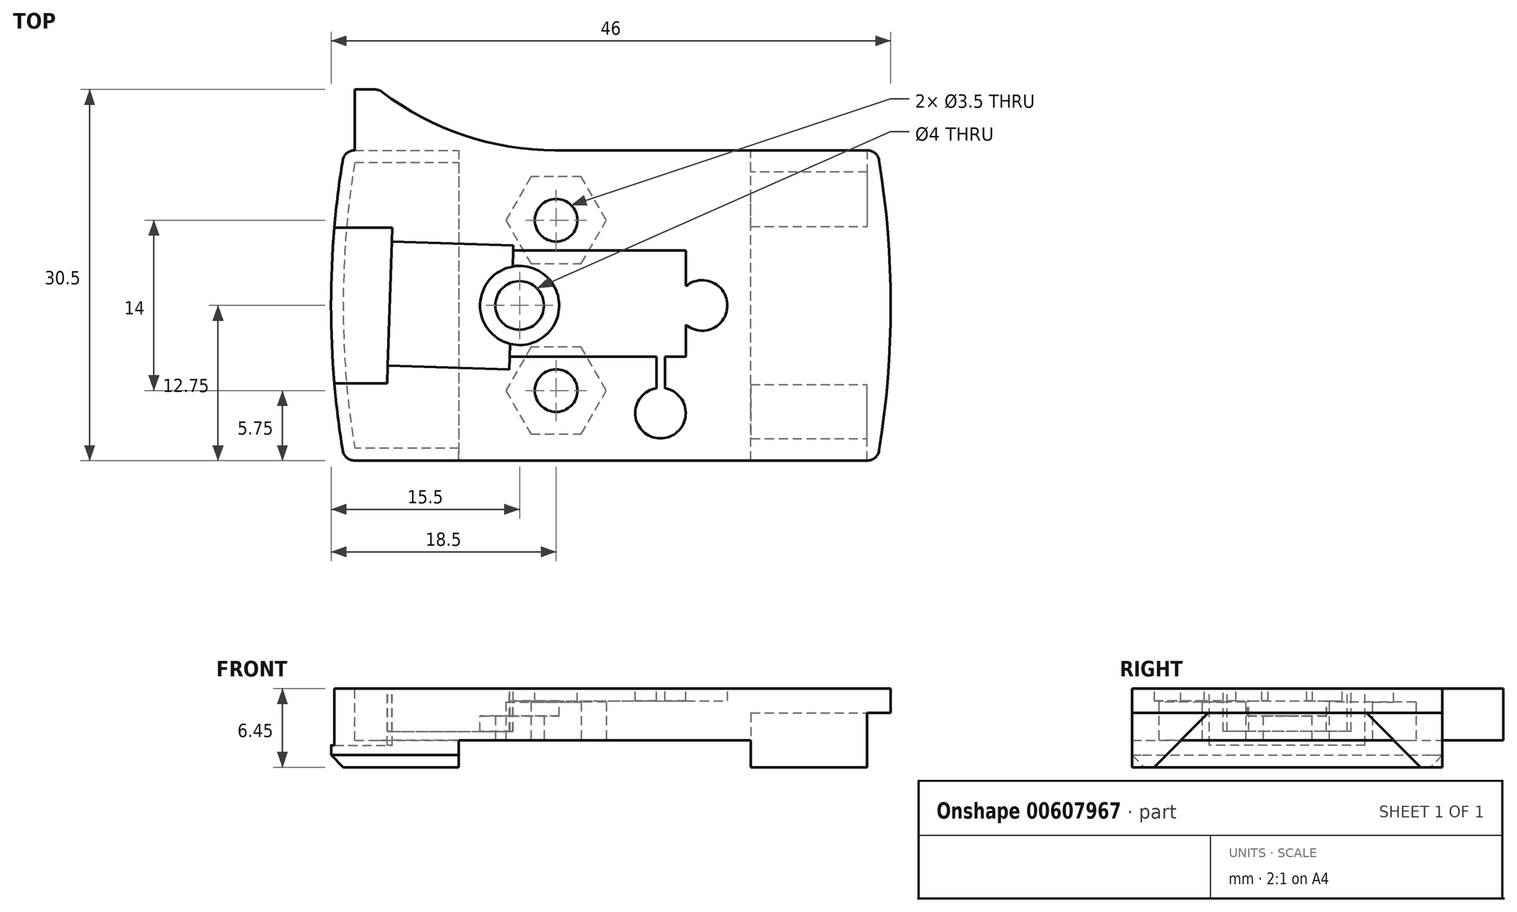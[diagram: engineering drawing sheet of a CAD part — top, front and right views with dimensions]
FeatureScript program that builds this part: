
annotation { "Feature Type Name" : "Feature", "Feature Type Description" : "" }
export const myFeature = defineFeature(function(context is Context, id is Id, definition is map)
    precondition{}
    {
        {
            var Q0;
            Q0=qCreatedBy(makeId("Top.planeOp"),FACE);
            var sketch = newSketch(context, id + "F0", { "sketchPlane" : qUnion([Q0])});
            skLineSegment(sketch, "E0.bottom", {"start": v(-21.9, 12.75) * mm, "end": v(21.9, 12.75) * mm});
            skLineSegment(sketch, "E0.top", {"start": v(-21.9, -12.75) * mm, "end": v(21.9, -12.75) * mm});
            skLineSegment(sketch, "E0.left", {"start": v(-22.4, 9.4) * mm, "end": v(-22.4, -12.75) * mm, "construction": true});
            skPoint(sketch, "E0.middle", {"position": v(0, 0) * mm});
            skArc(sketch, "E1", {"start": v(21.9, -12.75) * mm, "mid": v(23, 0) * mm, "end": v(21.9, 12.75) * mm});
            skPoint(sketch, "E2.orphan", {"position": v(22.4, 12.75) * mm});
            skPoint(sketch, "E0.right.end.orphan", {"position": v(22.4, -12.75) * mm});
            skArc(sketch, "E3.MirrorCS", {"start": v(-21.9, -12.75) * mm, "mid": v(-23, 0) * mm, "end": v(-21.9, 12.75) * mm});
            skPoint(sketch, "E4.orphan", {"position": v(-22.4, 12.75) * mm});
            skSolve(sketch);
        }
        {
            var Q0;
            Q0=makeQuery(id+"F0.imprint","IMPRINT",FACE,{"disambiguationData":[TD([[makeQuery(id+"F0.imprint","IMPRINT",EDGE,{"derivedFrom":sQuery(id+"F0.wireOp",EDGE,"E0.bottom")}),-1.0]])]});
            extrude(context, id + "F1", {"entities" : qUnion([Q0]), "depth" : 2 * mm, "offsetDistance" : 25 * mm});
        }
        {
            var Q0;
            Q0=makeQuery(id+"F1.opExtrude","SWEPT_EDGE",EDGE,{"disambiguationData":[OSD([sQuery(id+"F0.wireOp",EDGE,"E0.bottom"),sQuery(id+"F0.wireOp",EDGE,"E3.MirrorCS")])]});
            var Q1;
            Q1=makeQuery(id+"F1.opExtrude","SWEPT_EDGE",EDGE,{"disambiguationData":[OSD([sQuery(id+"F0.wireOp",EDGE,"E0.bottom"),sQuery(id+"F0.wireOp",EDGE,"E1")])]});
            var Q2;
            Q2=makeQuery(id+"F1.opExtrude","SWEPT_EDGE",EDGE,{"disambiguationData":[OSD([sQuery(id+"F0.wireOp",EDGE,"E0.top"),sQuery(id+"F0.wireOp",EDGE,"E3.MirrorCS")])]});
            var Q3;
            Q3=makeQuery(id+"F1.opExtrude","SWEPT_EDGE",EDGE,{"disambiguationData":[OSD([sQuery(id+"F0.wireOp",EDGE,"E0.top"),sQuery(id+"F0.wireOp",EDGE,"E1")])]});
            fillet(context, id + "F2", {"entities" : qUnion([Q0, Q1, Q2, Q3]), "radius" : 1 * mm, "tangentPropagation" : true, "allowEdgeOverflow" : false});
        }
        {
            var Q0;
            Q0=makeQuery(id+"F1.opExtrude","CAP_FACE",FACE,{"disambiguationData":[OSD([sQuery(id+"F0.wireOp",EDGE,"E0.bottom"),sQuery(id+"F0.wireOp",EDGE,"E0.top"),sQuery(id+"F0.wireOp",EDGE,"E1"),sQuery(id+"F0.wireOp",EDGE,"E3.MirrorCS")])],"isStart":true});
            var sketch = newSketch(context, id + "F3", { "sketchPlane" : qUnion([Q0])});
            skLineSegment(sketch, "E5.0", {"start": v(-21.06, 12.75) * mm, "end": v(21.06, 12.75) * mm});
            skArc(sketch, "E5.1", {"start": v(-21.06, 12.75) * mm, "mid": v(-21.7, 12.51) * mm, "end": v(-22.05, 11.9) * mm});
            skArc(sketch, "E5.2", {"start": v(-22.05, 11.9) * mm, "mid": v(-23, 0) * mm, "end": v(-22.05, -11.9) * mm});
            skArc(sketch, "E5.3", {"start": v(-22.05, -11.9) * mm, "mid": v(-21.7, -12.51) * mm, "end": v(-21.06, -12.75) * mm});
            skLineSegment(sketch, "E5.4", {"start": v(-21.06, -12.75) * mm, "end": v(21.06, -12.75) * mm});
            skLineSegment(sketch, "E6", {"start": v(11.5, 12.75) * mm, "end": v(11.5, -12.75) * mm});
            skSolve(sketch);
        }
        {
            var Q0;
            Q0 = qSketchRegion(id + "F3", true);
            extrude(context, id + "F4", {"entities" : qUnion([Q0]), "operationType" : NewBodyOperationType.ADD, "depth" : 2.25 * mm, "offsetDistance" : 25 * mm});
        }
        {
            var Q0;
            Q0=makeQuery(id+"F4.opExtrude","CAP_FACE",FACE,{"disambiguationData":[OSD([sQuery(id+"F3.wireOp",EDGE,"E5.0"),sQuery(id+"F3.wireOp",EDGE,"E5.1"),sQuery(id+"F3.wireOp",EDGE,"E5.2"),sQuery(id+"F3.wireOp",EDGE,"E5.3"),sQuery(id+"F3.wireOp",EDGE,"E5.4"),sQuery(id+"F3.wireOp",EDGE,"E6")])],"isStart":false});
            var sketch = newSketch(context, id + "F5", { "sketchPlane" : qUnion([Q0])});
            skLineSegment(sketch, "E7.0", {"start": v(-21.06, -12.75) * mm, "end": v(-12.5, -12.75) * mm});
            skArc(sketch, "E7.1", {"start": v(-22.05, 11.9) * mm, "mid": v(-23, 0) * mm, "end": v(-22.05, -11.9) * mm});
            skLineSegment(sketch, "E7.2", {"start": v(-21.06, 12.75) * mm, "end": v(-12.5, 12.75) * mm});
            skArc(sketch, "E7.3", {"start": v(-21.06, 12.75) * mm, "mid": v(-21.7, 12.51) * mm, "end": v(-22.05, 11.9) * mm});
            skArc(sketch, "E7.4", {"start": v(-22.05, -11.9) * mm, "mid": v(-21.7, -12.51) * mm, "end": v(-21.06, -12.75) * mm});
            skLineSegment(sketch, "E8", {"start": v(-12.5, -12.75) * mm, "end": v(-12.5, 12.75) * mm});
            skPoint(sketch, "E9.orphan", {"position": v(11.5, 12.75) * mm});
            skPoint(sketch, "E10.orphan", {"position": v(11.5, -12.75) * mm});
            skSolve(sketch);
        }
        {
            var Q0;
            Q0=makeQuery(id+"F5.imprint","IMPRINT",FACE,{"disambiguationData":[TD([[makeQuery(id+"F5.imprint","IMPRINT",EDGE,{"derivedFrom":sQuery(id+"F5.wireOp",EDGE,"E7.0")}),1.0]])]});
            extrude(context, id + "F6", {"entities" : qUnion([Q0]), "operationType" : NewBodyOperationType.ADD, "depth" : 2.2 * mm, "offsetDistance" : 25 * mm});
        }
        {
            var Q0;
            Q0=makeQuery(id+"F4.opExtrude","CAP_FACE",FACE,{"disambiguationData":[OSD([sQuery(id+"F3.wireOp",EDGE,"E5.0"),sQuery(id+"F3.wireOp",EDGE,"E5.1"),sQuery(id+"F3.wireOp",EDGE,"E5.2"),sQuery(id+"F3.wireOp",EDGE,"E5.3"),sQuery(id+"F3.wireOp",EDGE,"E5.4"),sQuery(id+"F3.wireOp",EDGE,"E6")])],"isStart":false});
            var sketch = newSketch(context, id + "F7", { "sketchPlane" : qUnion([Q0])});
            skCircle(sketch, "E11", {"center": v(-7.5, 0) * mm, "radius": 2 * mm});
            skSolve(sketch);
        }
        {
            var Q0;
            Q0=makeQuery(id+"F7.imprint","IMPRINT",FACE,{"disambiguationData":[TD([[makeQuery(id+"F7.imprint","IMPRINT",EDGE,{"derivedFrom":sQuery(id+"F7.wireOp",EDGE,"E11")}),1.0]])]});
            extrude(context, id + "F8", {"entities" : qUnion([Q0]), "operationType" : NewBodyOperationType.REMOVE, "oppositeDirection" : true, "depth" : 25 * mm, "offsetDistance" : 25 * mm});
        }
        {
            var Q0;
            Q0=makeQuery(id+"F1.opExtrude","CAP_FACE",FACE,{"disambiguationData":[OSD([sQuery(id+"F0.wireOp",EDGE,"E0.bottom"),sQuery(id+"F0.wireOp",EDGE,"E0.top"),sQuery(id+"F0.wireOp",EDGE,"E1"),sQuery(id+"F0.wireOp",EDGE,"E3.MirrorCS")])],"isStart":false});
            var sketch = newSketch(context, id + "F9", { "sketchPlane" : qUnion([Q0])});
            skCircle(sketch, "E12", {"center": v(-7.5, 0) * mm, "radius": 3.25 * mm});
            skSolve(sketch);
        }
        {
            var Q0;
            Q0=makeQuery(id+"F9.imprint","IMPRINT",FACE,{"disambiguationData":[TD([[makeQuery(id+"F9.imprint","IMPRINT",EDGE,{"derivedFrom":sQuery(id+"F9.wireOp",EDGE,"E12")}),1.0]])]});
            extrude(context, id + "F10", {"entities" : qUnion([Q0]), "operationType" : NewBodyOperationType.REMOVE, "oppositeDirection" : true, "depth" : 2.25 * mm, "offsetDistance" : 25 * mm});
        }
        {
            var Q0;
            Q0=makeQuery(id+"F1.opExtrude","CAP_FACE",FACE,{"disambiguationData":[OSD([sQuery(id+"F0.wireOp",EDGE,"E0.bottom"),sQuery(id+"F0.wireOp",EDGE,"E0.top"),sQuery(id+"F0.wireOp",EDGE,"E1"),sQuery(id+"F0.wireOp",EDGE,"E3.MirrorCS")])],"isStart":false});
            var sketch = newSketch(context, id + "F11", { "sketchPlane" : qUnion([Q0])});
            skLineSegment(sketch, "E13.bottom", {"start": v(-22.73, 6.4) * mm, "end": v(-17.98, 6.4) * mm});
            skLineSegment(sketch, "E13.top", {"start": v(-23.14, -6.4) * mm, "end": v(-18.39, -6.4) * mm});
            skLineSegment(sketch, "E13.right", {"start": v(-17.98, 6.4) * mm, "end": v(-18.39, -6.4) * mm});
            skPoint(sketch, "E13.middle", {"position": v(-20.56, 0) * mm});
            skLineSegment(sketch, "E14.bottom", {"start": v(-22.73, 6.4) * mm, "end": v(-24.9, 6.4) * mm});
            skLineSegment(sketch, "E14.top", {"start": v(-22.73, -6.4) * mm, "end": v(-24.9, -6.4) * mm});
            skLineSegment(sketch, "E14.left", {"start": v(-22.73, 6.4) * mm, "end": v(-22.73, -6.4) * mm});
            skLineSegment(sketch, "E14.right", {"start": v(-24.9, 6.4) * mm, "end": v(-24.9, -6.4) * mm});
            skSolve(sketch);
        }
        {
            var Q0;
            Q0=makeQuery(id+"F11.imprint","IMPRINT",FACE,{"disambiguationData":[TD([[makeQuery(id+"F11.imprint","IMPRINT",EDGE,{"derivedFrom":sQuery(id+"F11.wireOp",EDGE,"E13.bottom")}),-1.0]])]});
            var Q1;
            {var subQ0=sQuery(id+"F11.wireOp",EDGE,"E14.bottom");Q1=makeQuery(id+"F11.imprint","IMPRINT",FACE,{"disambiguationData":[TD([[makeQuery(id+"F11.imprint","IMPRINT",EDGE,{"derivedFrom":subQ0}),1.0]])]});}
            var Q2;
            Q2 = qSketchRegion(id + "F11", true);
            extrude(context, id + "F12", {"entities" : qUnion([Q0, Q1, Q2]), "operationType" : NewBodyOperationType.REMOVE, "oppositeDirection" : true, "depth" : 4.65 * mm, "offsetDistance" : 25 * mm});
        }
        {
            var Q0;
            Q0=makeQuery(id+"F1.opExtrude","CAP_FACE",FACE,{"disambiguationData":[OSD([sQuery(id+"F0.wireOp",EDGE,"E0.bottom"),sQuery(id+"F0.wireOp",EDGE,"E0.top"),sQuery(id+"F0.wireOp",EDGE,"E1"),sQuery(id+"F0.wireOp",EDGE,"E3.MirrorCS")])],"isStart":false});
            var sketch = newSketch(context, id + "F13", { "sketchPlane" : qUnion([Q0])});
            skLineSegment(sketch, "E15.bottom", {"start": v(-18.01, 5.26) * mm, "end": v(-8.02, 4.94) * mm});
            skLineSegment(sketch, "E15.top", {"start": v(-18.34, -4.94) * mm, "end": v(-8.35, -5.26) * mm});
            skLineSegment(sketch, "E15.left", {"start": v(-18.01, 5.26) * mm, "end": v(-18.34, -4.94) * mm});
            skLineSegment(sketch, "E15.right", {"start": v(-8.02, 4.94) * mm, "end": v(-8.35, -5.26) * mm});
            skPoint(sketch, "E15.middle", {"position": v(-13.18, 0) * mm});
            skSolve(sketch);
        }
        {
            var Q0;
            {var subQ1=sQuery(id+"F13.wireOp",EDGE,"E15.bottom");Q0=makeQuery(id+"F13.imprint","IMPRINT",FACE,{"disambiguationData":[TD([[makeQuery(id+"F13.imprint","IMPRINT",EDGE,{"derivedFrom":subQ1}),-1.0]])]});}
            extrude(context, id + "F14", {"entities" : qUnion([Q0]), "operationType" : NewBodyOperationType.REMOVE, "oppositeDirection" : true, "depth" : 3.5 * mm, "offsetDistance" : 25 * mm});
        }
        {
            var Q0;
            Q0=makeQuery(id+"F1.opExtrude","CAP_FACE",FACE,{"disambiguationData":[OSD([sQuery(id+"F0.wireOp",EDGE,"E0.bottom"),sQuery(id+"F0.wireOp",EDGE,"E0.top"),sQuery(id+"F0.wireOp",EDGE,"E1"),sQuery(id+"F0.wireOp",EDGE,"E3.MirrorCS")])],"isStart":false});
            var sketch = newSketch(context, id + "F15", { "sketchPlane" : qUnion([Q0])});
            skLineSegment(sketch, "E16", {"start": v(4.08, 12.75) * mm, "end": v(4.08, 8.85) * mm, "construction": true});
            skLineSegment(sketch, "E17", {"start": v(4.08, 8.85) * mm, "end": v(22.48, 8.85) * mm, "construction": true});
            skArc(sketch, "E18", {"start": v(7.9, -2.04) * mm, "mid": v(9.37, 0.9) * mm, "end": v(6.16, 1.58) * mm});
            skArc(sketch, "E19.MirrorCS", {"start": v(7.9, 2.04) * mm, "mid": v(9.37, -0.9) * mm, "end": v(6.16, -1.58) * mm});
            skLineSegment(sketch, "E20.MirrorCS", {"start": v(3.74, -4.22) * mm, "end": v(3.74, -6.8) * mm});
            skLineSegment(sketch, "E21.MirrorCS", {"start": v(4.08, -12.75) * mm, "end": v(4.08, -8.85) * mm, "construction": true});
            skLineSegment(sketch, "E22.MirrorCS", {"start": v(4.08, -8.85) * mm, "end": v(22.48, -8.85) * mm, "construction": true});
            skArc(sketch, "E23.MirrorCS", {"start": v(4.44, -6.8) * mm, "mid": v(4.07, -10.92) * mm, "end": v(3.74, -6.8) * mm});
            skLineSegment(sketch, "E24.MirrorCS", {"start": v(4.44, -4.22) * mm, "end": v(4.44, -6.8) * mm});
            skLineSegment(sketch, "E25.bottom", {"start": v(-8.31, -4.22) * mm, "end": v(3.74, -4.22) * mm});
            skLineSegment(sketch, "E25.top", {"start": v(-8.31, 4.5) * mm, "end": v(6.16, 4.5) * mm});
            skLineSegment(sketch, "E25.left", {"start": v(-8.31, -4.22) * mm, "end": v(-8.31, 4.5) * mm});
            skLineSegment(sketch, "E25.right", {"start": v(6.16, -4.22) * mm, "end": v(6.16, -1.58) * mm});
            skLineSegment(sketch, "E26.trimOffspring", {"start": v(4.44, -4.22) * mm, "end": v(6.16, -4.22) * mm});
            skLineSegment(sketch, "E27.trimOffspring", {"start": v(6.16, 1.58) * mm, "end": v(6.16, 4.5) * mm});
            skArc(sketch, "E28.trimOffspring", {"start": v(6.16, 1.58) * mm, "mid": v(6.65, 1.9) * mm, "end": v(7.2, 2.05) * mm});
            skArc(sketch, "E29.trimOffspring", {"start": v(6.16, -1.58) * mm, "mid": v(6.65, -1.9) * mm, "end": v(7.2, -2.05) * mm});
            skSolve(sketch);
        }
        {
            var Q0;
            Q0 = qSketchRegion(id + "F15", true);
            extrude(context, id + "F16", {"entities" : qUnion([Q0]), "operationType" : NewBodyOperationType.REMOVE, "oppositeDirection" : true, "depth" : 1 * mm, "offsetDistance" : 25 * mm});
        }
        {
            var Q0;
            Q0=makeQuery(id+"F1.opExtrude","CAP_FACE",FACE,{"disambiguationData":[OSD([sQuery(id+"F0.wireOp",EDGE,"E0.bottom"),sQuery(id+"F0.wireOp",EDGE,"E0.top"),sQuery(id+"F0.wireOp",EDGE,"E1"),sQuery(id+"F0.wireOp",EDGE,"E3.MirrorCS")])],"isStart":false});
            var sketch = newSketch(context, id + "F17", { "sketchPlane" : qUnion([Q0])});
            skCircle(sketch, "E30", {"center": v(-4.5, 7) * mm, "radius": 1.75 * mm});
            skCircle(sketch, "E31", {"center": v(-4.5, -7) * mm, "radius": 1.75 * mm});
            skLineSegment(sketch, "E32", {"start": v(-4.5, 7) * mm, "end": v(-4.5, -7) * mm, "construction": true});
            skLineSegment(sketch, "E33", {"start": v(-23.63, 0) * mm, "end": v(-4.5, 0) * mm, "construction": true});
            skSolve(sketch);
        }
        {
            var Q0;
            Q0=makeQuery(id+"F17.imprint","IMPRINT",FACE,{"disambiguationData":[TD([[makeQuery(id+"F17.imprint","IMPRINT",EDGE,{"derivedFrom":sQuery(id+"F17.wireOp",EDGE,"E30")}),1.0]])]});
            var Q1;
            Q1=makeQuery(id+"F17.imprint","IMPRINT",FACE,{"disambiguationData":[TD([[makeQuery(id+"F17.imprint","IMPRINT",EDGE,{"derivedFrom":sQuery(id+"F17.wireOp",EDGE,"E31")}),1.0]])]});
            extrude(context, id + "F18", {"entities" : qUnion([Q0, Q1]), "operationType" : NewBodyOperationType.REMOVE, "oppositeDirection" : true, "depth" : 25 * mm, "offsetDistance" : 25 * mm});
        }
        {
            var Q0;
            Q0=makeQuery(id+"F4.opExtrude","CAP_FACE",FACE,{"disambiguationData":[OSD([sQuery(id+"F3.wireOp",EDGE,"E5.0"),sQuery(id+"F3.wireOp",EDGE,"E5.1"),sQuery(id+"F3.wireOp",EDGE,"E5.2"),sQuery(id+"F3.wireOp",EDGE,"E5.3"),sQuery(id+"F3.wireOp",EDGE,"E5.4"),sQuery(id+"F3.wireOp",EDGE,"E6")])],"isStart":false});
            var sketch = newSketch(context, id + "F19", { "sketchPlane" : qUnion([Q0])});
            skCircle(sketch, "E34.cCircle", {"center": v(-4.5, 7) * mm, "radius": 3.58 * mm, "construction": true});
            skLineSegment(sketch, "E34.0", {"start": v(-6.56, 10.57) * mm, "end": v(-2.44, 10.57) * mm});
            skLineSegment(sketch, "E34.1", {"start": v(-2.44, 10.57) * mm, "end": v(-0.37, 7) * mm});
            skLineSegment(sketch, "E34.2", {"start": v(-0.37, 7) * mm, "end": v(-2.44, 3.42) * mm});
            skLineSegment(sketch, "E34.3", {"start": v(-2.44, 3.42) * mm, "end": v(-6.56, 3.42) * mm});
            skLineSegment(sketch, "E34.4", {"start": v(-6.56, 3.42) * mm, "end": v(-8.63, 7) * mm});
            skLineSegment(sketch, "E34.5", {"start": v(-8.63, 7) * mm, "end": v(-6.56, 10.57) * mm});
            skPoint(sketch, "E34.0.midPoint", {"position": v(-4.5, 10.57) * mm});
            skCircle(sketch, "E35.cCircle", {"center": v(-4.5, -7) * mm, "radius": 3.58 * mm, "construction": true});
            skLineSegment(sketch, "E35.0", {"start": v(-6.56, -3.43) * mm, "end": v(-2.44, -3.43) * mm});
            skLineSegment(sketch, "E35.1", {"start": v(-2.44, -3.43) * mm, "end": v(-0.37, -7) * mm});
            skLineSegment(sketch, "E35.2", {"start": v(-0.37, -7) * mm, "end": v(-2.44, -10.57) * mm});
            skLineSegment(sketch, "E35.3", {"start": v(-2.44, -10.57) * mm, "end": v(-6.56, -10.57) * mm});
            skLineSegment(sketch, "E35.4", {"start": v(-6.56, -10.58) * mm, "end": v(-8.63, -7) * mm});
            skLineSegment(sketch, "E35.5", {"start": v(-8.63, -7) * mm, "end": v(-6.56, -3.43) * mm});
            skPoint(sketch, "E35.0.midPoint", {"position": v(-4.5, -3.43) * mm});
            skSolve(sketch);
        }
        {
            var Q0;
            Q0 = qSketchRegion(id + "F19", true);
            extrude(context, id + "F20", {"entities" : qUnion([Q0]), "operationType" : NewBodyOperationType.REMOVE, "oppositeDirection" : true, "depth" : 3.15 * mm, "offsetDistance" : 25 * mm});
        }
        {
            var Q0;
            Q0=makeQuery(id+"F1.opExtrude","CAP_FACE",FACE,{"disambiguationData":[OSD([sQuery(id+"F0.wireOp",EDGE,"E0.bottom"),sQuery(id+"F0.wireOp",EDGE,"E0.top"),sQuery(id+"F0.wireOp",EDGE,"E1"),sQuery(id+"F0.wireOp",EDGE,"E3.MirrorCS")])],"isStart":true});
            var sketch = newSketch(context, id + "F21", { "sketchPlane" : qUnion([Q0])});
            skLineSegment(sketch, "E36.bottom", {"start": v(11.5, 12.75) * mm, "end": v(21.06, 12.75) * mm});
            skLineSegment(sketch, "E36.top", {"start": v(11.5, 6.5) * mm, "end": v(21.06, 6.5) * mm});
            skLineSegment(sketch, "E36.left", {"start": v(11.5, 12.75) * mm, "end": v(11.5, 6.5) * mm});
            skLineSegment(sketch, "E36.right", {"start": v(21.06, 12.75) * mm, "end": v(21.06, 6.5) * mm});
            skLineSegment(sketch, "E37.bottom", {"start": v(11.5, -12.75) * mm, "end": v(21.06, -12.75) * mm});
            skLineSegment(sketch, "E37.top", {"start": v(11.5, -6.5) * mm, "end": v(21.06, -6.5) * mm});
            skLineSegment(sketch, "E37.left", {"start": v(11.5, -12.75) * mm, "end": v(11.5, -6.5) * mm});
            skLineSegment(sketch, "E37.right", {"start": v(21.06, -12.75) * mm, "end": v(21.06, -6.5) * mm});
            skSolve(sketch);
        }
        {
            var Q0;
            Q0 = qSketchRegion(id + "F21", true);
            var Q1;
            Q1=makeQuery(id+"F6.opExtrude","CAP_FACE",FACE,{"disambiguationData":[OSD([sQuery(id+"F5.wireOp",EDGE,"E7.0"),sQuery(id+"F5.wireOp",EDGE,"E7.1"),sQuery(id+"F5.wireOp",EDGE,"E7.2"),sQuery(id+"F5.wireOp",EDGE,"E7.3"),sQuery(id+"F5.wireOp",EDGE,"E7.4"),sQuery(id+"F5.wireOp",EDGE,"E8")])],"isStart":false});
            extrude(context, id + "F22", {"entities" : qUnion([Q0]), "operationType" : NewBodyOperationType.ADD, "endBound" : BoundingType.UP_TO_SURFACE, "depth" : 25 * mm, "endBoundEntityFace" : qUnion([Q1]), "offsetDistance" : 25 * mm});
        }
        {
            var Q0;
            Q0=makeQuery(id+"F22.opExtrude","CAP_EDGE",EDGE,{"disambiguationData":[OSD([sQuery(id+"F21.wireOp",EDGE,"E36.top")])],"isStart":false});
            var Q1;
            Q1=makeQuery(id+"F22.opExtrude","CAP_EDGE",EDGE,{"disambiguationData":[OSD([sQuery(id+"F21.wireOp",EDGE,"E37.top")])],"isStart":false});
            chamfer(context, id + "F23", {"entities" : qUnion([Q0, Q1]), "width" : 4.45 * mm, "tangentPropagation" : true});
        }
        {
            var Q0;
            Q0=makeQuery(id+"F6.opExtrude","CAP_EDGE",EDGE,{"disambiguationData":[OSD([sQuery(id+"F5.wireOp",EDGE,"E7.2")])],"isStart":false});
            var Q1;
            Q1=makeQuery(id+"F6.opExtrude","CAP_EDGE",EDGE,{"disambiguationData":[OSD([sQuery(id+"F5.wireOp",EDGE,"E7.0")])],"isStart":false});
            chamfer(context, id + "F24", {"entities" : qUnion([Q0, Q1]), "width" : 1 * mm, "tangentPropagation" : true});
        }
        {
            var Q0;
            Q0=makeQuery(id+"F1.opExtrude","CAP_FACE",FACE,{"disambiguationData":[OSD([sQuery(id+"F0.wireOp",EDGE,"E0.bottom"),sQuery(id+"F0.wireOp",EDGE,"E0.top"),sQuery(id+"F0.wireOp",EDGE,"E1"),sQuery(id+"F0.wireOp",EDGE,"E3.MirrorCS")])],"isStart":false});
            var sketch = newSketch(context, id + "F25", { "sketchPlane" : qUnion([Q0])});
            skLineSegment(sketch, "E38", {"start": v(-21.06, 12.75) * mm, "end": v(-21.06, 17.75) * mm});
            skLineSegment(sketch, "E39", {"start": v(-21.06, 17.75) * mm, "end": v(-19.06, 17.75) * mm});
            skArc(sketch, "E40", {"start": v(-19.06, 17.75) * mm, "mid": v(-12.23, 14.04) * mm, "end": v(-4.56, 12.75) * mm});
            skLineSegment(sketch, "E41", {"start": v(-21.06, 12.75) * mm, "end": v(-4.56, 12.75) * mm});
            skSolve(sketch);
        }
        {
            var Q0;
            Q0=makeQuery(id+"F25.imprint","IMPRINT",FACE,{"disambiguationData":[TD([[makeQuery(id+"F25.imprint","IMPRINT",EDGE,{"derivedFrom":sQuery(id+"F25.wireOp",EDGE,"E38")}),-1.0]])]});
            var Q1;
            Q1=makeQuery(id+"F4.opExtrude","CAP_FACE",FACE,{"disambiguationData":[OSD([sQuery(id+"F3.wireOp",EDGE,"E5.0"),sQuery(id+"F3.wireOp",EDGE,"E5.1"),sQuery(id+"F3.wireOp",EDGE,"E5.2"),sQuery(id+"F3.wireOp",EDGE,"E5.3"),sQuery(id+"F3.wireOp",EDGE,"E5.4"),sQuery(id+"F3.wireOp",EDGE,"E6")])],"isStart":false});
            extrude(context, id + "F26", {"entities" : qUnion([Q0]), "operationType" : NewBodyOperationType.ADD, "endBound" : BoundingType.UP_TO_SURFACE, "oppositeDirection" : true, "depth" : 25 * mm, "endBoundEntityFace" : qUnion([Q1]), "offsetDistance" : 25 * mm});
        }
        {
            var Q0;
            Q0=makeQuery(id+"F26.opExtrude","SWEPT_EDGE",EDGE,{"disambiguationData":[OSD([sQuery(id+"F25.wireOp",EDGE,"E39"),sQuery(id+"F25.wireOp",EDGE,"E40")])]});
            fillet(context, id + "F27", {"entities" : qUnion([Q0]), "radius" : 1 * mm, "tangentPropagation" : true, "allowEdgeOverflow" : false});
        }
    });
